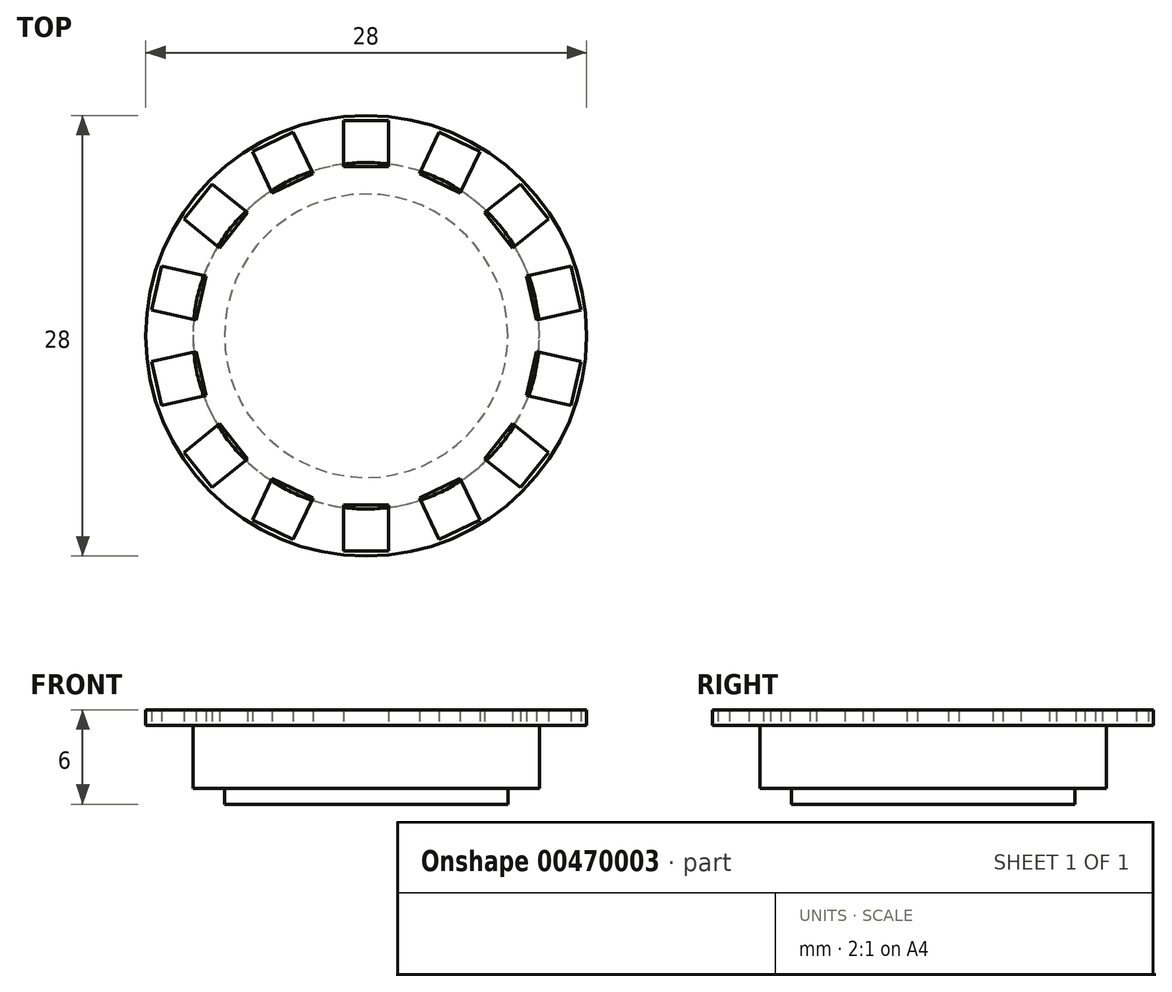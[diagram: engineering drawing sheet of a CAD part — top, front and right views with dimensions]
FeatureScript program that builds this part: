
annotation { "Feature Type Name" : "Feature", "Feature Type Description" : "" }
export const myFeature = defineFeature(function(context is Context, id is Id, definition is map)
    precondition{}
    {
        {
            var Q0;
            Q0=qCreatedBy(makeId("Top.planeOp"),FACE);
            var sketch = newSketch(context, id + "F0", { "sketchPlane" : qUnion([Q0])});
            skCircle(sketch, "E0", {"center": v(0, 0) * mm, "radius": 9 * mm});
            skSolve(sketch);
        }
        {
            var Q0;
            Q0 = qSketchRegion(id + "F0", true);
            extrude(context, id + "F1", {"entities" : qUnion([Q0]), "depth" : 1 * mm, "offsetDistance" : 25 * mm});
        }
        {
            var Q0;
            Q0=qCreatedBy(makeId("Top.planeOp"),FACE);
            cPlane(context, id + "F2", {"entities" : qUnion([Q0]), "cplaneType" : CPlaneType.OFFSET, "offset" : 1 * mm, "width" : 150 * mm, "height" : 150 * mm});
        }
        {
            var Q0;
            Q0=qCreatedBy(id+"F2.planeOp",FACE);
            var sketch = newSketch(context, id + "F3", { "sketchPlane" : qUnion([Q0])});
            skCircle(sketch, "E1", {"center": v(0, 0) * mm, "radius": 11 * mm});
            skSolve(sketch);
        }
        {
            var Q0;
            Q0 = qSketchRegion(id + "F3", true);
            extrude(context, id + "F4", {"entities" : qUnion([Q0]), "operationType" : NewBodyOperationType.ADD, "depth" : 4 * mm, "offsetDistance" : 25 * mm});
        }
        {
            var Q0;
            Q0=qCreatedBy(id+"F2.planeOp",FACE);
            cPlane(context, id + "F5", {"entities" : qUnion([Q0]), "cplaneType" : CPlaneType.OFFSET, "offset" : 4 * mm, "width" : 150 * mm, "height" : 150 * mm});
        }
        {
            var Q0;
            Q0=qCreatedBy(id+"F5.planeOp",FACE);
            var sketch = newSketch(context, id + "F6", { "sketchPlane" : qUnion([Q0])});
            skCircle(sketch, "E2", {"center": v(0, 0) * mm, "radius": 14 * mm});
            skCircle(sketch, "E3", {"center": v(0, 0) * mm, "radius": 13 * mm});
            skLineSegment(sketch, "E4.bottom", {"start": v(1.43, 10.76) * mm, "end": v(-1.43, 10.76) * mm});
            skLineSegment(sketch, "E4.top", {"start": v(1.43, 13.67) * mm, "end": v(-1.43, 13.67) * mm});
            skLineSegment(sketch, "E4.left", {"start": v(1.43, 10.76) * mm, "end": v(1.43, 13.67) * mm});
            skLineSegment(sketch, "E4.right", {"start": v(-1.43, 10.76) * mm, "end": v(-1.43, 13.67) * mm});
            skPoint(sketch, "E4.middle", {"position": v(0, 12.21) * mm});
            skPoint(sketch, "E5.1.0", {"position": v(-5.3, 11) * mm});
            skLineSegment(sketch, "E5.1.1", {"start": v(-3.38, 10.32) * mm, "end": v(-4.64, 12.93) * mm});
            skLineSegment(sketch, "E5.1.2", {"start": v(-3.38, 10.32) * mm, "end": v(-5.96, 9.07) * mm});
            skLineSegment(sketch, "E5.1.3", {"start": v(-5.96, 9.07) * mm, "end": v(-7.22, 11.7) * mm});
            skLineSegment(sketch, "E5.1.4", {"start": v(-4.64, 12.93) * mm, "end": v(-7.22, 11.7) * mm});
            skPoint(sketch, "E5.2.0", {"position": v(-9.55, 7.61) * mm});
            skLineSegment(sketch, "E5.2.1", {"start": v(-7.52, 7.83) * mm, "end": v(-9.79, 9.64) * mm});
            skLineSegment(sketch, "E5.2.2", {"start": v(-7.52, 7.83) * mm, "end": v(-9.3, 5.59) * mm});
            skLineSegment(sketch, "E5.2.3", {"start": v(-9.3, 5.59) * mm, "end": v(-11.58, 7.4) * mm});
            skLineSegment(sketch, "E5.2.4", {"start": v(-9.79, 9.64) * mm, "end": v(-11.58, 7.4) * mm});
            skPoint(sketch, "E5.3.0", {"position": v(-11.9, 2.72) * mm});
            skLineSegment(sketch, "E5.3.1", {"start": v(-10.17, 3.8) * mm, "end": v(-13, 4.44) * mm});
            skLineSegment(sketch, "E5.3.2", {"start": v(-10.17, 3.8) * mm, "end": v(-10.8, 1) * mm});
            skLineSegment(sketch, "E5.3.3", {"start": v(-10.8, 1) * mm, "end": v(-13.64, 1.64) * mm});
            skLineSegment(sketch, "E5.3.4", {"start": v(-13, 4.44) * mm, "end": v(-13.64, 1.64) * mm});
            skPoint(sketch, "E5.4.0", {"position": v(-11.9, -2.72) * mm});
            skLineSegment(sketch, "E5.4.1", {"start": v(-10.8, -1) * mm, "end": v(-13.64, -1.64) * mm});
            skLineSegment(sketch, "E5.4.2", {"start": v(-10.8, -1) * mm, "end": v(-10.17, -3.8) * mm});
            skLineSegment(sketch, "E5.4.3", {"start": v(-10.17, -3.8) * mm, "end": v(-13, -4.44) * mm});
            skLineSegment(sketch, "E5.4.4", {"start": v(-13.64, -1.64) * mm, "end": v(-13, -4.44) * mm});
            skPoint(sketch, "E5.5.0", {"position": v(-9.55, -7.61) * mm});
            skLineSegment(sketch, "E5.5.1", {"start": v(-9.3, -5.59) * mm, "end": v(-11.58, -7.4) * mm});
            skLineSegment(sketch, "E5.5.2", {"start": v(-9.3, -5.59) * mm, "end": v(-7.52, -7.83) * mm});
            skLineSegment(sketch, "E5.5.3", {"start": v(-7.52, -7.83) * mm, "end": v(-9.79, -9.64) * mm});
            skLineSegment(sketch, "E5.5.4", {"start": v(-11.58, -7.4) * mm, "end": v(-9.79, -9.64) * mm});
            skPoint(sketch, "E5.6.0", {"position": v(-5.3, -11) * mm});
            skLineSegment(sketch, "E5.6.1", {"start": v(-5.96, -9.07) * mm, "end": v(-7.22, -11.7) * mm});
            skLineSegment(sketch, "E5.6.2", {"start": v(-5.96, -9.07) * mm, "end": v(-3.38, -10.32) * mm});
            skLineSegment(sketch, "E5.6.3", {"start": v(-3.38, -10.32) * mm, "end": v(-4.64, -12.93) * mm});
            skLineSegment(sketch, "E5.6.4", {"start": v(-7.22, -11.7) * mm, "end": v(-4.64, -12.93) * mm});
            skPoint(sketch, "E5.7.0", {"position": v(0, -12.21) * mm});
            skLineSegment(sketch, "E5.7.1", {"start": v(-1.43, -10.76) * mm, "end": v(-1.43, -13.67) * mm});
            skLineSegment(sketch, "E5.7.2", {"start": v(-1.43, -10.76) * mm, "end": v(1.43, -10.76) * mm});
            skLineSegment(sketch, "E5.7.3", {"start": v(1.43, -10.76) * mm, "end": v(1.43, -13.67) * mm});
            skLineSegment(sketch, "E5.7.4", {"start": v(-1.43, -13.67) * mm, "end": v(1.43, -13.67) * mm});
            skPoint(sketch, "E5.8.0", {"position": v(5.3, -11) * mm});
            skLineSegment(sketch, "E5.8.1", {"start": v(3.38, -10.32) * mm, "end": v(4.64, -12.93) * mm});
            skLineSegment(sketch, "E5.8.2", {"start": v(3.38, -10.32) * mm, "end": v(5.96, -9.07) * mm});
            skLineSegment(sketch, "E5.8.3", {"start": v(5.96, -9.07) * mm, "end": v(7.22, -11.7) * mm});
            skLineSegment(sketch, "E5.8.4", {"start": v(4.64, -12.93) * mm, "end": v(7.22, -11.7) * mm});
            skPoint(sketch, "E5.9.0", {"position": v(9.55, -7.61) * mm});
            skLineSegment(sketch, "E5.9.1", {"start": v(7.52, -7.83) * mm, "end": v(9.79, -9.64) * mm});
            skLineSegment(sketch, "E5.9.2", {"start": v(7.52, -7.83) * mm, "end": v(9.3, -5.59) * mm});
            skLineSegment(sketch, "E5.9.3", {"start": v(9.3, -5.59) * mm, "end": v(11.58, -7.4) * mm});
            skLineSegment(sketch, "E5.9.4", {"start": v(9.79, -9.64) * mm, "end": v(11.58, -7.4) * mm});
            skPoint(sketch, "E5.10.0", {"position": v(11.9, -2.72) * mm});
            skLineSegment(sketch, "E5.10.1", {"start": v(10.17, -3.8) * mm, "end": v(13, -4.44) * mm});
            skLineSegment(sketch, "E5.10.2", {"start": v(10.17, -3.8) * mm, "end": v(10.8, -1) * mm});
            skLineSegment(sketch, "E5.10.3", {"start": v(10.8, -1) * mm, "end": v(13.64, -1.64) * mm});
            skLineSegment(sketch, "E5.10.4", {"start": v(13, -4.44) * mm, "end": v(13.64, -1.64) * mm});
            skPoint(sketch, "E5.11.0", {"position": v(11.9, 2.72) * mm});
            skLineSegment(sketch, "E5.11.1", {"start": v(10.8, 1) * mm, "end": v(13.64, 1.64) * mm});
            skLineSegment(sketch, "E5.11.2", {"start": v(10.8, 1) * mm, "end": v(10.17, 3.8) * mm});
            skLineSegment(sketch, "E5.11.3", {"start": v(10.17, 3.8) * mm, "end": v(13, 4.44) * mm});
            skLineSegment(sketch, "E5.11.4", {"start": v(13.64, 1.64) * mm, "end": v(13, 4.44) * mm});
            skPoint(sketch, "E5.12.0", {"position": v(9.55, 7.61) * mm});
            skLineSegment(sketch, "E5.12.1", {"start": v(9.3, 5.59) * mm, "end": v(11.58, 7.4) * mm});
            skLineSegment(sketch, "E5.12.2", {"start": v(9.3, 5.59) * mm, "end": v(7.52, 7.83) * mm});
            skLineSegment(sketch, "E5.12.3", {"start": v(7.52, 7.83) * mm, "end": v(9.79, 9.64) * mm});
            skLineSegment(sketch, "E5.12.4", {"start": v(11.58, 7.4) * mm, "end": v(9.79, 9.64) * mm});
            skPoint(sketch, "E5.13.0", {"position": v(5.3, 11) * mm});
            skLineSegment(sketch, "E5.13.1", {"start": v(5.96, 9.07) * mm, "end": v(7.22, 11.7) * mm});
            skLineSegment(sketch, "E5.13.2", {"start": v(5.96, 9.07) * mm, "end": v(3.38, 10.32) * mm});
            skLineSegment(sketch, "E5.13.3", {"start": v(3.38, 10.32) * mm, "end": v(4.64, 12.93) * mm});
            skLineSegment(sketch, "E5.13.4", {"start": v(7.22, 11.7) * mm, "end": v(4.64, 12.93) * mm});
            skSolve(sketch);
        }
        {
            var Q0;
            Q0 = qSketchRegion(id + "F6", true);
            var Q1;
            {var subQ53=sQuery(id+"F6.wireOp",EDGE,"E4.bottom");Q1=makeQuery(id+"F6.imprint","IMPRINT",FACE,{"disambiguationData":[TD([[makeQuery(id+"F6.imprint","IMPRINT",EDGE,{"derivedFrom":subQ53}),1.0]])]});}
            extrude(context, id + "F7", {"entities" : qUnion([Q0, Q1]), "operationType" : NewBodyOperationType.ADD, "depth" : 1 * mm, "offsetDistance" : 25 * mm});
        }
    });
